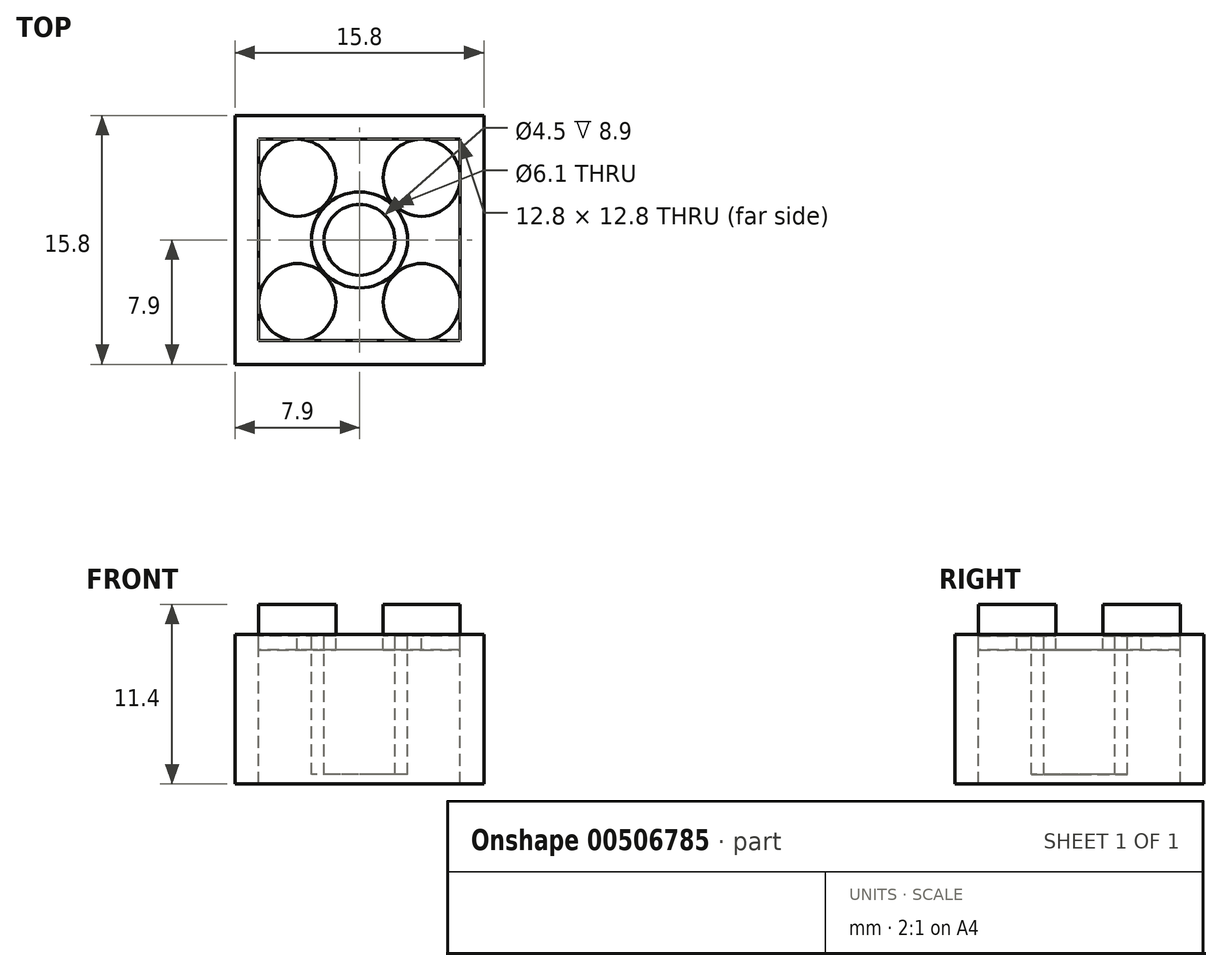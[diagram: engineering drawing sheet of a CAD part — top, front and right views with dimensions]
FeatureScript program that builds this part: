
annotation { "Feature Type Name" : "Feature", "Feature Type Description" : "" }
export const myFeature = defineFeature(function(context is Context, id is Id, definition is map)
    precondition{}
    {
        {
            var Q0;
            Q0=qCreatedBy(makeId("Top.planeOp"),FACE);
            var sketch = newSketch(context, id + "F0", { "sketchPlane" : qUnion([Q0])});
            skLineSegment(sketch, "E0.bottom", {"start": v(7.9, 7.9) * mm, "end": v(-7.9, 7.9) * mm});
            skLineSegment(sketch, "E0.top", {"start": v(7.9, -7.9) * mm, "end": v(-7.9, -7.9) * mm});
            skLineSegment(sketch, "E0.left", {"start": v(7.9, 7.9) * mm, "end": v(7.9, -7.9) * mm});
            skLineSegment(sketch, "E0.right", {"start": v(-7.9, 7.9) * mm, "end": v(-7.9, -7.9) * mm});
            skPoint(sketch, "E0.middle", {"position": v(0, 0) * mm});
            skLineSegment(sketch, "E1.bottom", {"start": v(6.4, 6.4) * mm, "end": v(-6.4, 6.4) * mm});
            skLineSegment(sketch, "E1.top", {"start": v(6.4, -6.4) * mm, "end": v(-6.4, -6.4) * mm});
            skLineSegment(sketch, "E1.left", {"start": v(6.4, 6.4) * mm, "end": v(6.4, -6.4) * mm});
            skLineSegment(sketch, "E1.right", {"start": v(-6.4, 6.4) * mm, "end": v(-6.4, -6.4) * mm});
            skCircle(sketch, "E2", {"center": v(-3.95, 3.95) * mm, "radius": 2.45 * mm});
            skCircle(sketch, "E3", {"center": v(-3.95, -3.95) * mm, "radius": 2.45 * mm});
            skCircle(sketch, "E4", {"center": v(3.95, 3.95) * mm, "radius": 2.45 * mm});
            skCircle(sketch, "E5", {"center": v(3.95, -3.95) * mm, "radius": 2.45 * mm});
            skCircle(sketch, "E6", {"center": v(0, 0) * mm, "radius": 2.25 * mm});
            skCircle(sketch, "E7", {"center": v(0, 0) * mm, "radius": 3.05 * mm});
            skSolve(sketch);
        }
        {
            var Q0;
            Q0=makeQuery(id+"F0.imprint","IMPRINT",FACE,{"disambiguationData":[TD([[makeQuery(id+"F0.imprint","IMPRINT",EDGE,{"derivedFrom":sQuery(id+"F0.wireOp",EDGE,"E0.bottom")}),1.0]])]});
            extrude(context, id + "F1", {"entities" : qUnion([Q0]), "oppositeDirection" : true, "depth" : 9.5 * mm});
        }
        {
            var Q0;
            {var subQ5=sQuery(id+"F0.wireOp",EDGE,"E4");var subQ13=sQuery(id+"F0.wireOp",EDGE,"E1.bottom");var subQ14=makeQuery(id+"F0.imprint","INTERSECT",VERTEX,{"derivedFrom":[subQ13,subQ5]});Q0=makeQuery(id+"F0.imprint","IMPRINT",FACE,{"disambiguationData":[TD([[makeQuery(id+"F0.imprint","IMPRINT",EDGE,{"disambiguationData":[TD([[subQ14,-1.0]])],"derivedFrom":subQ13}),1.0]])]});}
            var Q1;
            {var subQ0=sQuery(id+"F0.wireOp",EDGE,"E1.right");var subQ1=sQuery(id+"F0.wireOp",EDGE,"E1.bottom");var subQ2=makeQuery(id+"F0.imprint","INTERSECT",VERTEX,{"derivedFrom":[subQ1,subQ0]});Q1=makeQuery(id+"F0.imprint","IMPRINT",FACE,{"disambiguationData":[TD([[makeQuery(id+"F0.imprint","IMPRINT",EDGE,{"disambiguationData":[TD([[subQ2,1.0]])],"derivedFrom":subQ1}),1.0]])]});}
            var Q2;
            {var subQ0=sQuery(id+"F0.wireOp",EDGE,"E1.left");var subQ1=sQuery(id+"F0.wireOp",EDGE,"E1.bottom");var subQ2=makeQuery(id+"F0.imprint","INTERSECT",VERTEX,{"derivedFrom":[subQ1,subQ0]});Q2=makeQuery(id+"F0.imprint","IMPRINT",FACE,{"disambiguationData":[TD([[makeQuery(id+"F0.imprint","IMPRINT",EDGE,{"disambiguationData":[TD([[subQ2,-1.0]])],"derivedFrom":subQ1}),1.0]])]});}
            var Q3;
            {var subQ0=sQuery(id+"F0.wireOp",EDGE,"E1.left");var subQ1=sQuery(id+"F0.wireOp",EDGE,"E1.top");var subQ2=makeQuery(id+"F0.imprint","INTERSECT",VERTEX,{"derivedFrom":[subQ1,subQ0]});Q3=makeQuery(id+"F0.imprint","IMPRINT",FACE,{"disambiguationData":[TD([[makeQuery(id+"F0.imprint","IMPRINT",EDGE,{"disambiguationData":[TD([[subQ2,-1.0]])],"derivedFrom":subQ1}),-1.0]])]});}
            var Q4;
            {var subQ0=sQuery(id+"F0.wireOp",EDGE,"E1.right");var subQ1=sQuery(id+"F0.wireOp",EDGE,"E1.top");var subQ2=makeQuery(id+"F0.imprint","INTERSECT",VERTEX,{"derivedFrom":[subQ1,subQ0]});Q4=makeQuery(id+"F0.imprint","IMPRINT",FACE,{"disambiguationData":[TD([[makeQuery(id+"F0.imprint","IMPRINT",EDGE,{"disambiguationData":[TD([[subQ2,1.0]])],"derivedFrom":subQ1}),-1.0]])]});}
            var Q5;
            Q5=makeQuery(id+"F0.imprint","IMPRINT",FACE,{"disambiguationData":[TD([[makeQuery(id+"F0.imprint","IMPRINT",EDGE,{"derivedFrom":sQuery(id+"F0.wireOp",EDGE,"E6")}),1.0]])]});
            extrude(context, id + "F2", {"entities" : qUnion([Q0, Q1, Q2, Q3, Q4, Q5]), "oppositeDirection" : true, "depth" : 1 * mm});
        }
        {
            var Q0;
            {var subQ0=sQuery(id+"F0.wireOp",EDGE,"E3");var subQ1=makeQuery(id+"F0.imprint","INTERSECT",VERTEX,{"derivedFrom":[sQuery(id+"F0.wireOp",EDGE,"E1.top"),subQ0]});Q0=makeQuery(id+"F0.imprint","IMPRINT",FACE,{"disambiguationData":[TD([[makeQuery(id+"F0.imprint","IMPRINT",EDGE,{"disambiguationData":[TD([[subQ1,1.0]])],"derivedFrom":subQ0}),1.0]])]});}
            var Q1;
            {var subQ0=sQuery(id+"F0.wireOp",EDGE,"E2");var subQ1=makeQuery(id+"F0.imprint","INTERSECT",VERTEX,{"derivedFrom":[sQuery(id+"F0.wireOp",EDGE,"E1.bottom"),subQ0]});Q1=makeQuery(id+"F0.imprint","IMPRINT",FACE,{"disambiguationData":[TD([[makeQuery(id+"F0.imprint","IMPRINT",EDGE,{"disambiguationData":[TD([[subQ1,-1.0]])],"derivedFrom":subQ0}),1.0]])]});}
            var Q2;
            {var subQ0=sQuery(id+"F0.wireOp",EDGE,"E4");var subQ1=makeQuery(id+"F0.imprint","INTERSECT",VERTEX,{"derivedFrom":[sQuery(id+"F0.wireOp",EDGE,"E1.bottom"),subQ0]});Q2=makeQuery(id+"F0.imprint","IMPRINT",FACE,{"disambiguationData":[TD([[makeQuery(id+"F0.imprint","IMPRINT",EDGE,{"disambiguationData":[TD([[subQ1,1.0]])],"derivedFrom":subQ0}),1.0]])]});}
            var Q3;
            {var subQ0=sQuery(id+"F0.wireOp",EDGE,"E5");var subQ1=makeQuery(id+"F0.imprint","INTERSECT",VERTEX,{"derivedFrom":[sQuery(id+"F0.wireOp",EDGE,"E1.top"),subQ0]});Q3=makeQuery(id+"F0.imprint","IMPRINT",FACE,{"disambiguationData":[TD([[makeQuery(id+"F0.imprint","IMPRINT",EDGE,{"disambiguationData":[TD([[subQ1,1.0]])],"derivedFrom":subQ0}),1.0]])]});}
            extrude(context, id + "F3", {"entities" : qUnion([Q0, Q1, Q2, Q3]), "depth" : 1.9 * mm, "hasSecondDirection" : true, "secondDirectionOppositeDirection" : true, "secondDirectionDepth" : .1 * mm});
        }
        {
            var Q0;
            Q0=makeQuery(id+"F0.imprint","IMPRINT",FACE,{"disambiguationData":[TD([[makeQuery(id+"F0.imprint","IMPRINT",EDGE,{"derivedFrom":sQuery(id+"F0.wireOp",EDGE,"E6")}),-1.0]])]});
            extrude(context, id + "F4", {"entities" : qUnion([Q0]), "oppositeDirection" : true, "depth" : 8.9 * mm});
        }
    });
